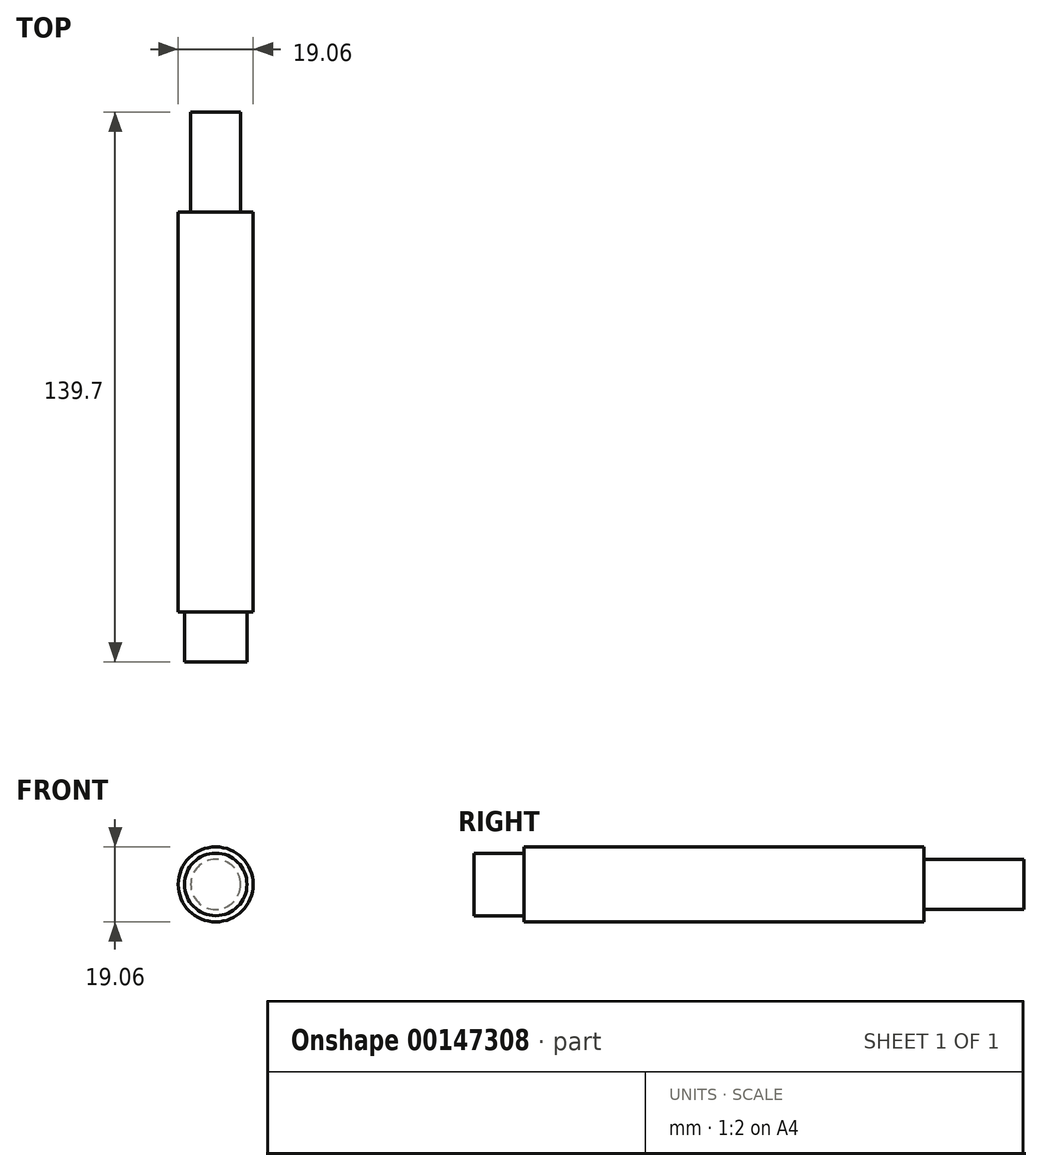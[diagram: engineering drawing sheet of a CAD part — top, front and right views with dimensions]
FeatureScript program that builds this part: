
annotation { "Feature Type Name" : "Feature", "Feature Type Description" : "" }
export const myFeature = defineFeature(function(context is Context, id is Id, definition is map)
    precondition{}
    {
        {
            var Q0;
            Q0=qCreatedBy(makeId("Front.planeOp"),FACE);
            var sketch = newSketch(context, id + "F0", { "sketchPlane" : qUnion([Q0])});
            skCircle(sketch, "E0", {"center": v(0, 0) * mm, "radius": 9.53 * mm});
            skSolve(sketch);
        }
        {
            var Q0;
            Q0 = qSketchRegion(id + "F0", true);
            extrude(context, id + "F1", {"entities" : qUnion([Q0]), "depth" : 101.6 * mm});
        }
        {
            var Q0;
            Q0=qCreatedBy(makeId("Front.planeOp"),FACE);
            var sketch = newSketch(context, id + "F2", { "sketchPlane" : qUnion([Q0])});
            skCircle(sketch, "E1", {"center": v(0, 0) * mm, "radius": 6.35 * mm});
            skSolve(sketch);
        }
        {
            var Q0;
            Q0 = qSketchRegion(id + "F2", true);
            extrude(context, id + "F3", {"entities" : qUnion([Q0]), "operationType" : NewBodyOperationType.ADD, "oppositeDirection" : true, "depth" : 25.4 * mm});
        }
        {
            var Q0;
            Q0=makeQuery(id+"F1.opExtrude","CAP_FACE",FACE,{"disambiguationData":[OSD([sQuery(id+"F0.wireOp",EDGE,"E0")])],"isStart":false});
            var sketch = newSketch(context, id + "F4", { "sketchPlane" : qUnion([Q0])});
            skCircle(sketch, "E2", {"center": v(0, 0) * mm, "radius": 7.94 * mm});
            skSolve(sketch);
        }
        {
            var Q0;
            Q0 = qSketchRegion(id + "F4", true);
            extrude(context, id + "F5", {"entities" : qUnion([Q0]), "operationType" : NewBodyOperationType.ADD, "depth" : 12.7 * mm});
        }
    });
